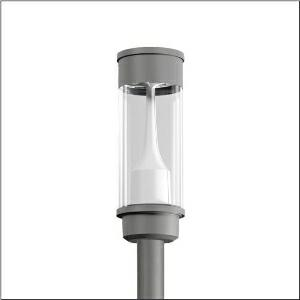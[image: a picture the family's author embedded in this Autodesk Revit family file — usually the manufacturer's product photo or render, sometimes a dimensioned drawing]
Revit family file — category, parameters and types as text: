
# Revit family: litepole_iq___st1_2a_5xa5415mf14hp_8171
name_source: partatom
category: Lighting Fixtures
units: mm (PartAtom-declared; Revit-internal decimal feet)

## family parameters
Cut with Voids When Loaded = No
Host = Face
Light Source = No
Part Type = Normal
Room Calculation Point = No
Round Connector Dimension = Use Diameter
Shared = No

## types (1)
- --- (1 x LED, 4240 lm, 33.6 W, 2700K)
    Apparent Load = 34 VA
    CIE Flux Codes = 22 60 93 95 100
    Color Rendering = 70
    Color Temperature = 2700K
    Default Elevation = 1800 mm
    Description = Litepole iQ, mast luminaire, Module 540 iQ-SR, primary light control with 3 zone facetted reflector, of plastic, silver coated, highly specular, structured, primary optical cover: cover, of PMMA, transparent, partly coated, light distribution: ST1.2a, light emission: direct distribution, primary light characteristic: asymmetric, installation type: post-top, LED, High Power LED, rated luminous flux: 4.240lm, luminous efficacy: 126lm/W, light colour: 727, colour temperature: 2700K, control gear: iQ Street-Remote, control: optimised constant luminous flux control (CLO 2.0), Desk-Remote (wireless, voltage-free reading and setting of iQ features in the workshop via application-optimized NFC function/RFID function), Light-Fading, Smart-Wire, Night-Set, Lumen-Switch, Temp-Guard, Auto-Match, Street-Remote, pre-setting: logarithmic dimming characteristic, with terminal, 6-pole, max. 2.5mm², mains connection: 230..240V, AC, 50/60Hz, start of lifetime: 34W, end of service life: 36W, reduction: 15W, luminaire housing, upper part, of glass-fibre reinforced polyester, coated, Siteco® metallic grey (DB 702S), diameter: 210mm, height: 590mm, spigot size: d x l = 76 x 70mm (post-top) | with reducer (optional accessory) 60 x 70mm, mounting height: 3..5m, post-top mast mounting element, of diecast aluminium, coated, Siteco® metallic grey (DB 702S), Module 540 iQ-SR, traffic white (RAL 9016), equipment: Power, protection rating (complete): IP65, insulation class (complete): insulation class II (safety insulation), certification: CE, ENEC, VDE, packaging unit: 1 piece

Light Distribution: ST1.2a
    Height = 590 mm
    Lamp = 1 x LED
    Lamp Light Flux = 4240 lm
    Lamp Power = 33.6 W
    Lamp count = 1
    Length = 220 mm
    Luminous efficacy = 126 lm/W
    Manufacturer = Siteco
    ModVariant = No
    Model = 5XA5415MF14HP
    Number of Poles = 1
    OnlyDefault = Yes
    Power Factor = 1
    Product Name = Litepole iQ | ST1.2a
    Product group = mast luminaire | pylon top
    ProductGroupID = 6100
    Protection Class = Protection class II
    Protection Degree = IP 65
    RLX_Detail_Level = 1
    RLX_Emergency_Light_Flux = 0 lm
    RLX_Emergency_Type = 0
    RLX_Emergency_Type_DB = No
    RlxData = <blob elided: 29749 chars, md5=8296c03e>
    Socket = socket
    Standby Power = 0 W
    System Light Flux = 4240 lm
    System Power = 34 W
    Type Comments = factory setting: luminous flux: 100 % | dim-lin: 254 | 695 mA
    Type Image = l_1006025.jpg
    URL = http://relux.com
    VarID = @adj_152992
    Voltage = 0 V
    Weight = 0.00 kg
    Width = 0 mm  [stored 0 ft]

note: [stored X ft] marks values corroborated as IEEE doubles in the binary element streams (Revit-internal decimal feet)

## geometry (parser evidence)
native form markers: Blend x4, Sweep x12
no freeform markers — native parametric forms only
